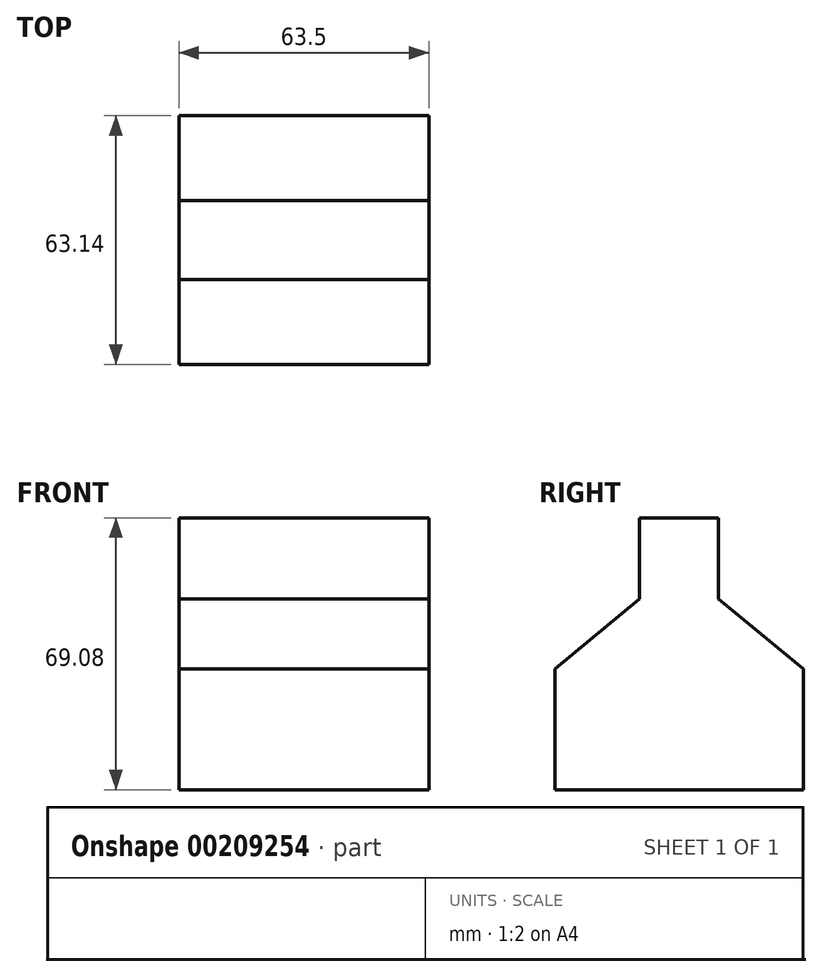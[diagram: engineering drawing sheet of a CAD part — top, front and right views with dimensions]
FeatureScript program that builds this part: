
annotation { "Feature Type Name" : "Feature", "Feature Type Description" : "" }
export const myFeature = defineFeature(function(context is Context, id is Id, definition is map)
    precondition{}
    {
        {
            var Q0;
            Q0=qCreatedBy(makeId("Right.planeOp"),FACE);
            var sketch = newSketch(context, id + "F0", { "sketchPlane" : qUnion([Q0])});
            skLineSegment(sketch, "E0.bottom", {"start": v(31.57, -40.8) * mm, "end": v(-31.57, -40.8) * mm});
            skLineSegment(sketch, "E0.left", {"start": v(31.57, -40.8) * mm, "end": v(31.57, -10.16) * mm});
            skLineSegment(sketch, "E0.right", {"start": v(-31.57, -40.8) * mm, "end": v(-31.57, -10.16) * mm});
            skPoint(sketch, "E0.middle", {"position": v(0, -25.48) * mm});
            skLineSegment(sketch, "E1", {"start": v(31.57, -10.16) * mm, "end": v(10, 7.66) * mm});
            skLineSegment(sketch, "E2", {"start": v(10, 7.66) * mm, "end": v(10, 28.29) * mm});
            skLineSegment(sketch, "E3", {"start": v(10, 28.29) * mm, "end": v(0, 28.29) * mm});
            skLineSegment(sketch, "E4.MirrorCS", {"start": v(-10, 28.29) * mm, "end": v(0, 28.29) * mm});
            skLineSegment(sketch, "E5.MirrorCS", {"start": v(-10, 7.66) * mm, "end": v(-10, 28.29) * mm});
            skLineSegment(sketch, "E6.MirrorCS", {"start": v(-31.57, -10.16) * mm, "end": v(-10, 7.66) * mm});
            skSolve(sketch);
        }
        {
            var Q0;
            Q0=makeQuery(id+"F0.imprint","IMPRINT",FACE,{"disambiguationData":[TD([[makeQuery(id+"F0.imprint","IMPRINT",EDGE,{"derivedFrom":sQuery(id+"F0.wireOp",EDGE,"E0.bottom")}),-1.0]])]});
            extrude(context, id + "F1", {"entities" : qUnion([Q0]), "endBound" : BoundingType.SYMMETRIC, "depth" : 63.5 * mm});
        }
    });
